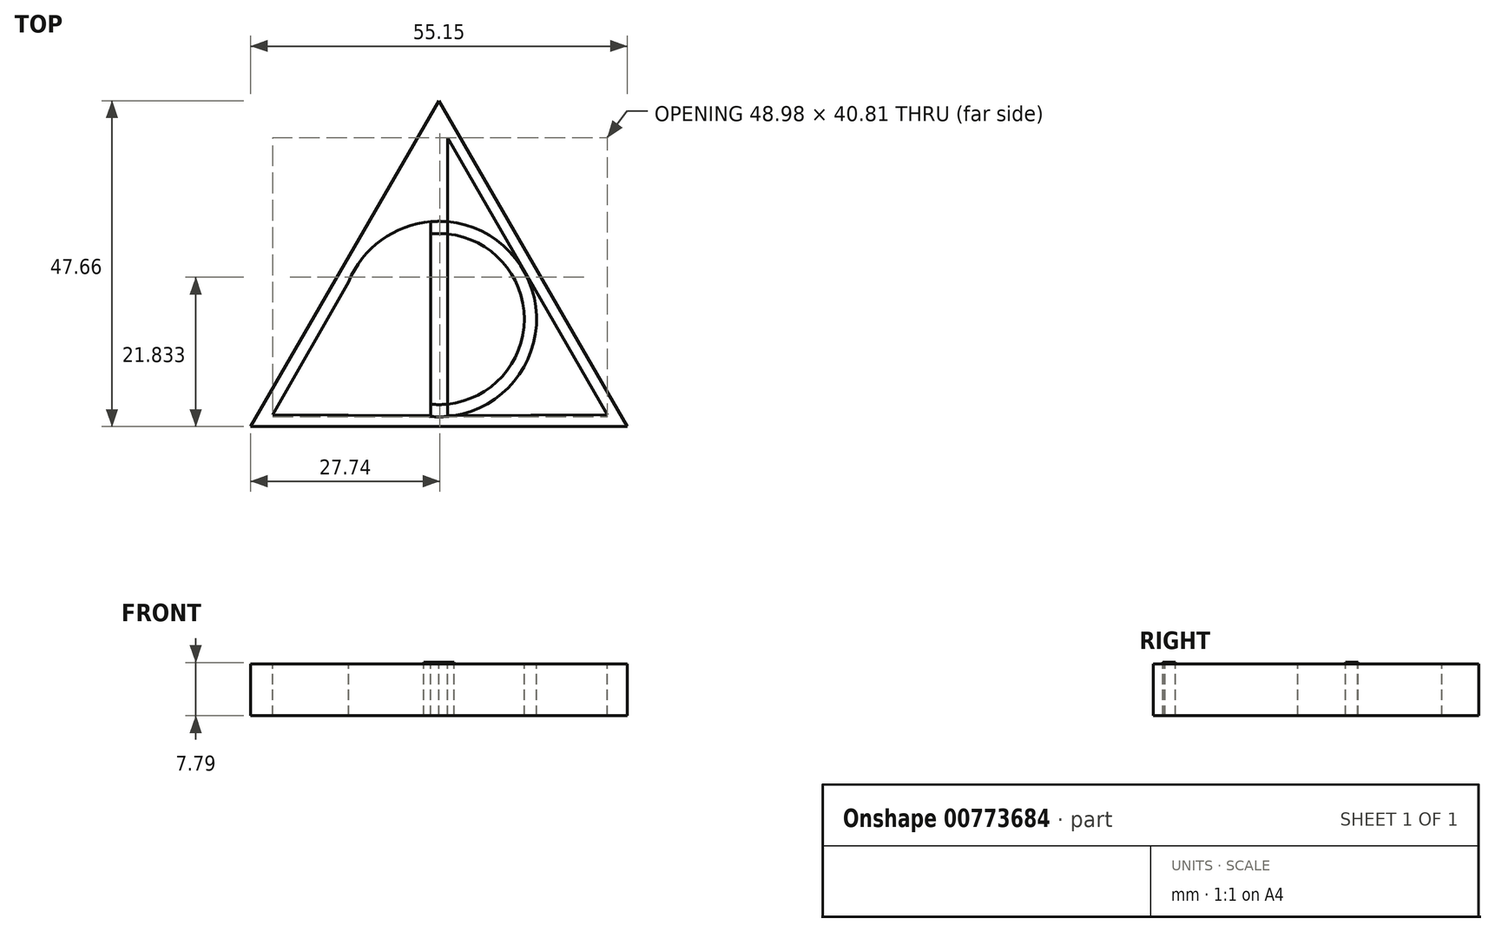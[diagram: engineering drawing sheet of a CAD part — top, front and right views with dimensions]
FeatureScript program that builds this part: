
annotation { "Feature Type Name" : "Feature", "Feature Type Description" : "" }
export const myFeature = defineFeature(function(context is Context, id is Id, definition is map)
    precondition{}
    {
        {
            var Q0;
            Q0=qCreatedBy(makeId("Top.planeOp"),FACE);
            var sketch = newSketch(context, id + "F0", { "sketchPlane" : qUnion([Q0])});
            skLineSegment(sketch, "E0", {"start": v(-0.55, 30.48) * mm, "end": v(-28.16, -17.18) * mm});
            skPoint(sketch, "E0.startSnap0", {"position": v(-0.55, 31.37) * mm});
            skLineSegment(sketch, "E1", {"start": v(-24.91, -15.46) * mm, "end": v(-1.76, 25.06) * mm});
            skLineSegment(sketch, "E2", {"start": v(-1.76, 25.06) * mm, "end": v(-1.76, -15.59) * mm});
            skLineSegment(sketch, "E3", {"start": v(-1.76, -15.59) * mm, "end": v(-24.91, -15.46) * mm});
            skLineSegment(sketch, "E4", {"start": v(0.69, 25.06) * mm, "end": v(0.69, -15.59) * mm});
            skLineSegment(sketch, "E5", {"start": v(0.69, -15.59) * mm, "end": v(24.07, -15.46) * mm});
            skLineSegment(sketch, "E6", {"start": v(24.07, -15.46) * mm, "end": v(0.69, 25.06) * mm});
            skLineSegment(sketch, "E7", {"start": v(-28.16, -17.18) * mm, "end": v(27, -17.18) * mm});
            skLineSegment(sketch, "E8", {"start": v(27, -17.18) * mm, "end": v(-0.55, 30.48) * mm});
            skCircle(sketch, "E9", {"center": v(-0.58, -1.46) * mm, "radius": 12.51 * mm});
            skPoint(sketch, "E9.first.point", {"position": v(0.69, 10.99) * mm});
            skPoint(sketch, "E9.second.point", {"position": v(0.69, -13.9) * mm});
            skPoint(sketch, "E9.third.point", {"position": v(-7.44, -11.93) * mm});
            skCircle(sketch, "E10", {"center": v(-0.59, -1.46) * mm, "radius": 12.51 * mm});
            skCircle(sketch, "E11", {"center": v(-0.58, -1.46) * mm, "radius": 14.3 * mm});
            skSolve(sketch);
        }
        {
            var Q0;
            Q0=makeQuery(id+"F0.imprint","IMPRINT",FACE,{"disambiguationData":[TD([[makeQuery(id+"F0.imprint","IMPRINT",EDGE,{"derivedFrom":sQuery(id+"F0.wireOp",EDGE,"E0")}),1.0]])]});
            var Q1;
            {var subQ5=sQuery(id+"F0.wireOp",EDGE,"TyAsRICD-otik-V24Q-ElQ1-bTIZRVe9MeHP");var subQ6=sQuery(id+"F0.wireOp",EDGE,"E1");var subQ7=makeQuery(id+"F0.imprint","INTERSECT",VERTEX,{"disambiguationData":[OD(0.0)],"derivedFrom":[subQ6,subQ5]});Q1=makeQuery(id+"F0.imprint","IMPRINT",FACE,{"disambiguationData":[TD([[makeQuery(id+"F0.imprint","IMPRINT",EDGE,{"disambiguationData":[TD([[subQ7,-1.0]])],"derivedFrom":subQ6}),-1.0]])]});}
            var Q2;
            {var subQ0=sQuery(id+"F0.wireOp",EDGE,"TyAsRICD-otik-V24Q-ElQ1-bTIZRVe9MeHP");var subQ5=sQuery(id+"F0.wireOp",EDGE,"E4");var subQ10=makeQuery(id+"F0.imprint","INTERSECT",VERTEX,{"derivedFrom":[subQ5,subQ0]});Q2=makeQuery(id+"F0.imprint","IMPRINT",FACE,{"disambiguationData":[TD([[makeQuery(id+"F0.imprint","IMPRINT",EDGE,{"disambiguationData":[TD([[subQ10,-1.0]])],"derivedFrom":subQ5}),1.0]])]});}
            var Q3;
            {var subQ0=sQuery(id+"F0.wireOp",EDGE,"E9");var subQ1=sQuery(id+"F0.wireOp",EDGE,"E2");var subQ5=makeQuery(id+"F0.imprint","INTERSECT",VERTEX,{"disambiguationData":[OD(0.0)],"derivedFrom":[subQ1,subQ0]});Q3=makeQuery(id+"F0.imprint","IMPRINT",FACE,{"disambiguationData":[TD([[makeQuery(id+"F0.imprint","IMPRINT",EDGE,{"disambiguationData":[TD([[subQ5,-1.0]])],"derivedFrom":subQ1}),1.0]])]});}
            var Q4;
            {var subQ1=sQuery(id+"F0.wireOp",EDGE,"E4");var subQ6=sQuery(id+"F0.wireOp",EDGE,"E11");var subQ8=makeQuery(id+"F0.imprint","INTERSECT",VERTEX,{"derivedFrom":[subQ1,subQ6]});Q4=makeQuery(id+"F0.imprint","IMPRINT",FACE,{"disambiguationData":[TD([[makeQuery(id+"F0.imprint","IMPRINT",EDGE,{"disambiguationData":[TD([[subQ8,-1.0]])],"derivedFrom":subQ1}),1.0]])]});}
            extrude(context, id + "F1", {"entities" : qUnion([Q0, Q1, Q2, Q3, Q4]), "oppositeDirection" : true, "depth" : 7.54 * mm, "offsetDistance" : 25.4 * mm});
        }
        {
            var Q0;
            {var subQ7=sQuery(id+"F0.wireOp",EDGE,"E3");var subQ9=sQuery(id+"F0.wireOp",EDGE,"E2");var subQ10=makeQuery(id+"F0.imprint","INTERSECT",VERTEX,{"derivedFrom":[subQ9,subQ7]});Q0=makeQuery(id+"F0.imprint","IMPRINT",FACE,{"disambiguationData":[TD([[makeQuery(id+"F0.imprint","IMPRINT",EDGE,{"disambiguationData":[TD([[subQ10,1.0]])],"derivedFrom":subQ9}),1.0]])]});}
            var Q1;
            {var subQ5=sQuery(id+"F0.wireOp",EDGE,"E11");var subQ7=sQuery(id+"F0.wireOp",EDGE,"E2");var subQ8=makeQuery(id+"F0.imprint","INTERSECT",VERTEX,{"derivedFrom":[subQ7,subQ5]});Q1=makeQuery(id+"F0.imprint","IMPRINT",FACE,{"disambiguationData":[TD([[makeQuery(id+"F0.imprint","IMPRINT",EDGE,{"disambiguationData":[TD([[subQ8,-1.0]])],"derivedFrom":subQ7}),1.0]])]});}
            extrude(context, id + "F2", {"entities" : qUnion([Q0, Q1]), "depth" : 0.25 * mm, "offsetDistance" : 25.4 * mm});
        }
    });
